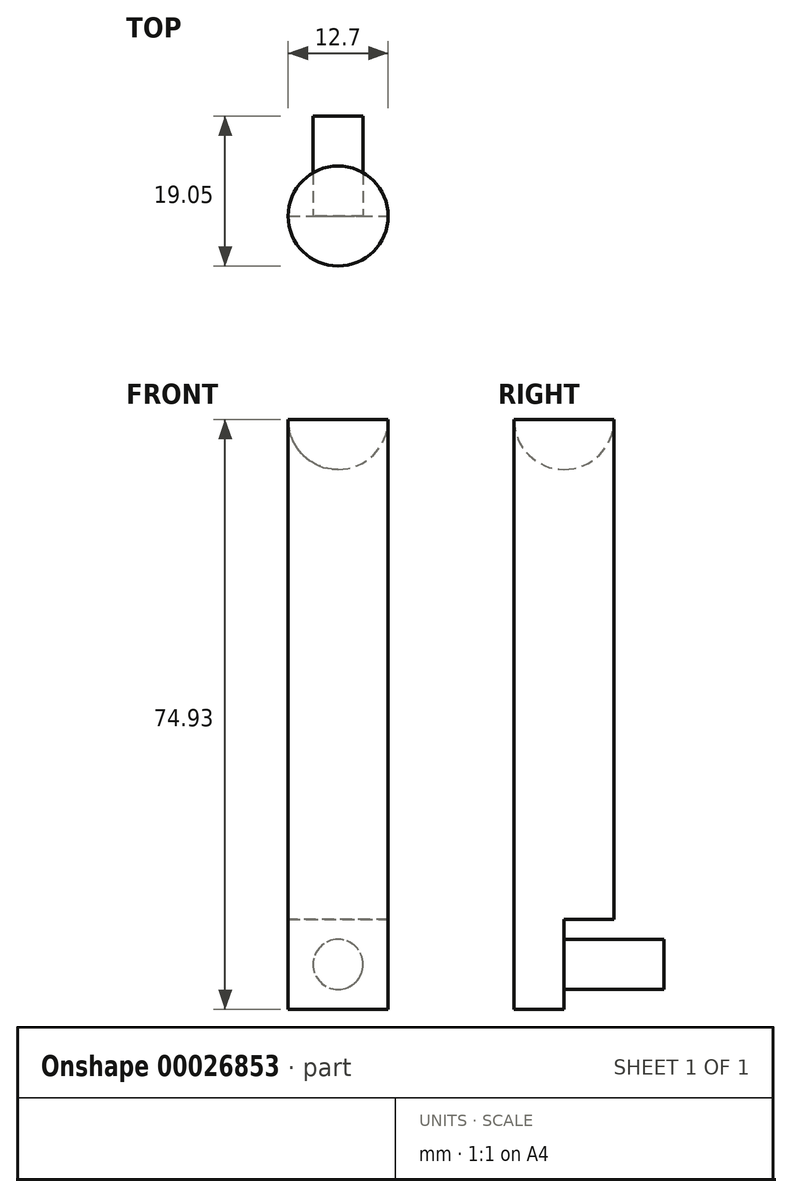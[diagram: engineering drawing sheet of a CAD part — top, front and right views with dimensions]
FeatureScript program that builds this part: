
annotation { "Feature Type Name" : "Feature", "Feature Type Description" : "" }
export const myFeature = defineFeature(function(context is Context, id is Id, definition is map)
    precondition{}
    {
        {
            var Q0;
            Q0=qCreatedBy(makeId("Front.planeOp"),FACE);
            var sketch = newSketch(context, id + "F0", { "sketchPlane" : qUnion([Q0])});
            skLineSegment(sketch, "E0.top", {"start": v(0, -13.25) * mm, "end": v(6.35, -13.25) * mm});
            skLineSegment(sketch, "E0.left", {"start": v(0, 43.9) * mm, "end": v(0, -13.25) * mm});
            skLineSegment(sketch, "E0.right", {"start": v(6.35, 50.25) * mm, "end": v(6.35, -13.25) * mm});
            skArc(sketch, "E1", {"start": v(0, 43.9) * mm, "mid": v(4.5, 45.76) * mm, "end": v(6.35, 50.25) * mm});
            skSolve(sketch);
        }
        {
            var Q0;
            Q0=makeQuery(id+"F0.imprint","IMPRINT",FACE,{"disambiguationData":[TD([[makeQuery(id+"F0.imprint","IMPRINT",EDGE,{"derivedFrom":sQuery(id+"F0.wireOp",EDGE,"E0.top")}),1.0]])]});
            var Q1;
            Q1=sQuery(id+"F0.wireOp",EDGE,"E0.left");
            revolve(context, id + "F1", {"entities" : qUnion([Q0]), "axis" : qUnion([Q1]), "revolveType" : RevolveType.FULL});
        }
        {
            var Q0;
            Q0=makeQuery(id+"F1.opRevolve","SWEPT_FACE",FACE,{"disambiguationData":[OSD([sQuery(id+"F0.wireOp",EDGE,"E0.top")])]});
            var sketch = newSketch(context, id + "F2", { "sketchPlane" : qUnion([Q0])});
            skLineSegment(sketch, "E2", {"start": v(-6.35, 0) * mm, "end": v(6.35, 0) * mm});
            skSolve(sketch);
        }
        {
            var Q0;
            {var subQ1=sQuery(id+"F2.wireOp",EDGE,"E2");Q0=makeQuery(id+"F2.imprint","IMPRINT",FACE,{"disambiguationData":[TD([[makeQuery(id+"F2.imprint","IMPRINT",EDGE,{"derivedFrom":subQ1}),1.0]])]});}
            extrude(context, id + "F3", {"entities" : qUnion([Q0]), "operationType" : NewBodyOperationType.ADD, "depth" : 11.43 * mm});
        }
        {
            var Q0;
            Q0=makeQuery(id+"F3.opExtrude","SWEPT_FACE",FACE,{"disambiguationData":[OSD([sQuery(id+"F2.wireOp",EDGE,"E2")])]});
            var sketch = newSketch(context, id + "F4", { "sketchPlane" : qUnion([Q0])});
            skCircle(sketch, "E3", {"center": v(0, -18.96) * mm, "radius": 3.18 * mm});
            skPoint(sketch, "E4.start.orphan", {"position": v(-6.35, -18.96) * mm});
            skPoint(sketch, "E5.end.orphan", {"position": v(0, -24.68) * mm});
            skPoint(sketch, "E5.start.orphan", {"position": v(6.35, -18.96) * mm});
            skSolve(sketch);
        }
        {
            var Q0;
            Q0=makeQuery(id+"F4.imprint","IMPRINT",FACE,{"disambiguationData":[TD([[makeQuery(id+"F4.imprint","IMPRINT",EDGE,{"derivedFrom":sQuery(id+"F4.wireOp",EDGE,"E3")}),1.0]])]});
            extrude(context, id + "F5", {"entities" : qUnion([Q0]), "operationType" : NewBodyOperationType.ADD, "depth" : 12.7 * mm});
        }
    });
